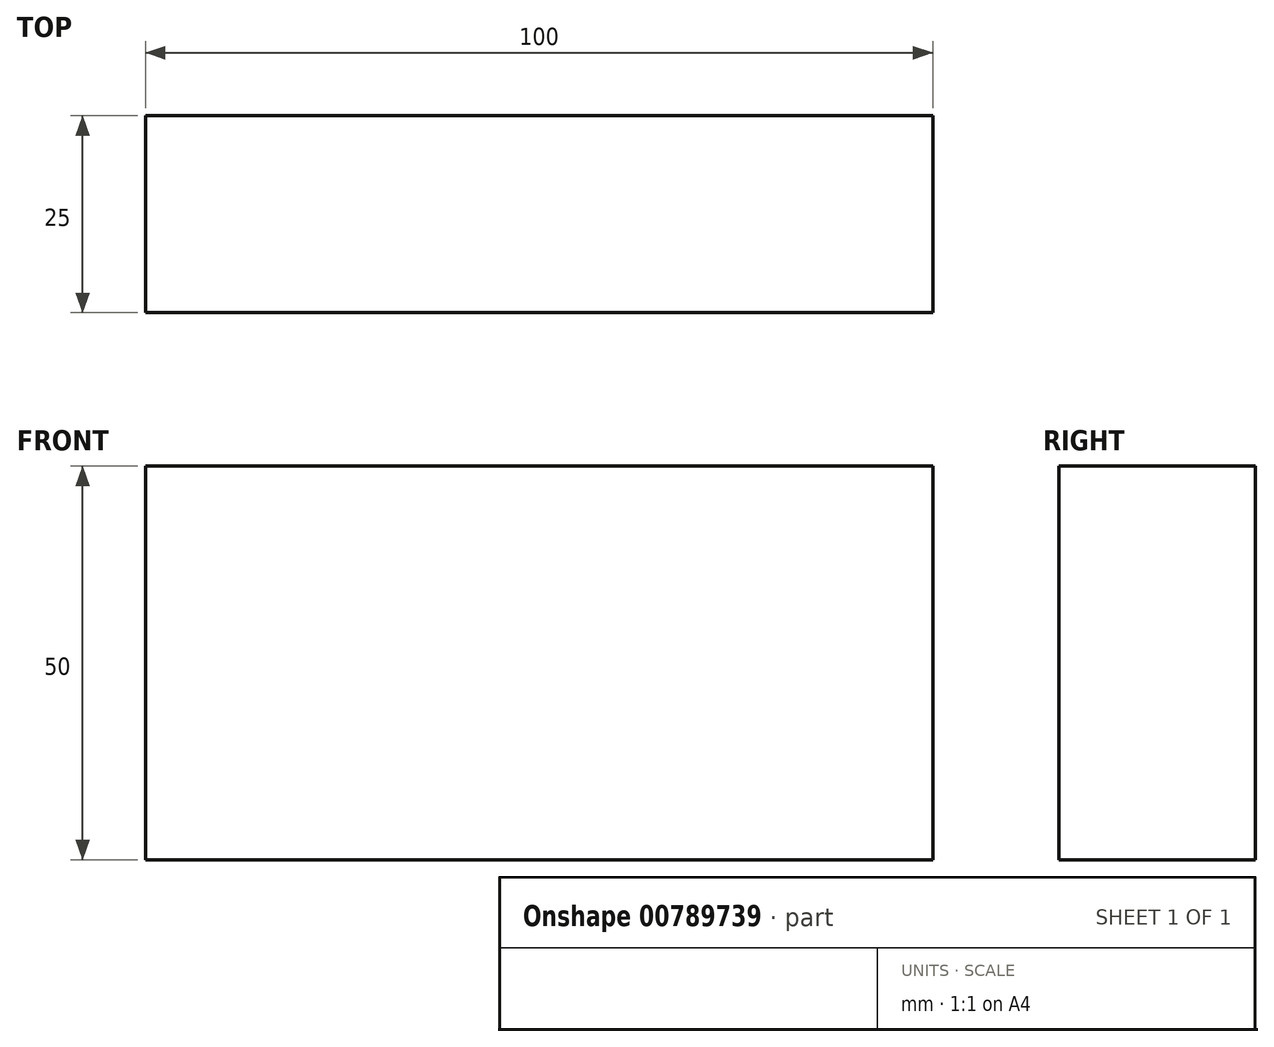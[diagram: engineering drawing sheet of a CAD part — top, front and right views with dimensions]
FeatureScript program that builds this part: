
annotation { "Feature Type Name" : "Feature", "Feature Type Description" : "" }
export const myFeature = defineFeature(function(context is Context, id is Id, definition is map)
    precondition{}
    {
        {
            var Q0;
            Q0=qCreatedBy(makeId("Front.planeOp"),FACE);
            var sketch = newSketch(context, id + "F0", { "sketchPlane" : qUnion([Q0])});
            skLineSegment(sketch, "E0.bottom", {"start": v(50, -25) * mm, "end": v(-50, -25) * mm});
            skLineSegment(sketch, "E0.top", {"start": v(50, 25) * mm, "end": v(-50, 25) * mm});
            skLineSegment(sketch, "E0.left", {"start": v(50, -25) * mm, "end": v(50, 25) * mm});
            skLineSegment(sketch, "E0.right", {"start": v(-50, -25) * mm, "end": v(-50, 25) * mm});
            skPoint(sketch, "E0.middle", {"position": v(0, 0) * mm});
            skSolve(sketch);
        }
        {
            var Q0;
            Q0=makeQuery(id+"F0.imprint","IMPRINT",FACE,{"disambiguationData":[TD([[makeQuery(id+"F0.imprint","IMPRINT",EDGE,{"derivedFrom":sQuery(id+"F0.wireOp",EDGE,"E0.bottom")}),-1.0]])]});
            extrude(context, id + "F1", {"entities" : qUnion([Q0]), "depth" : 25 * mm, "offsetDistance" : 25 * mm});
        }
    });
